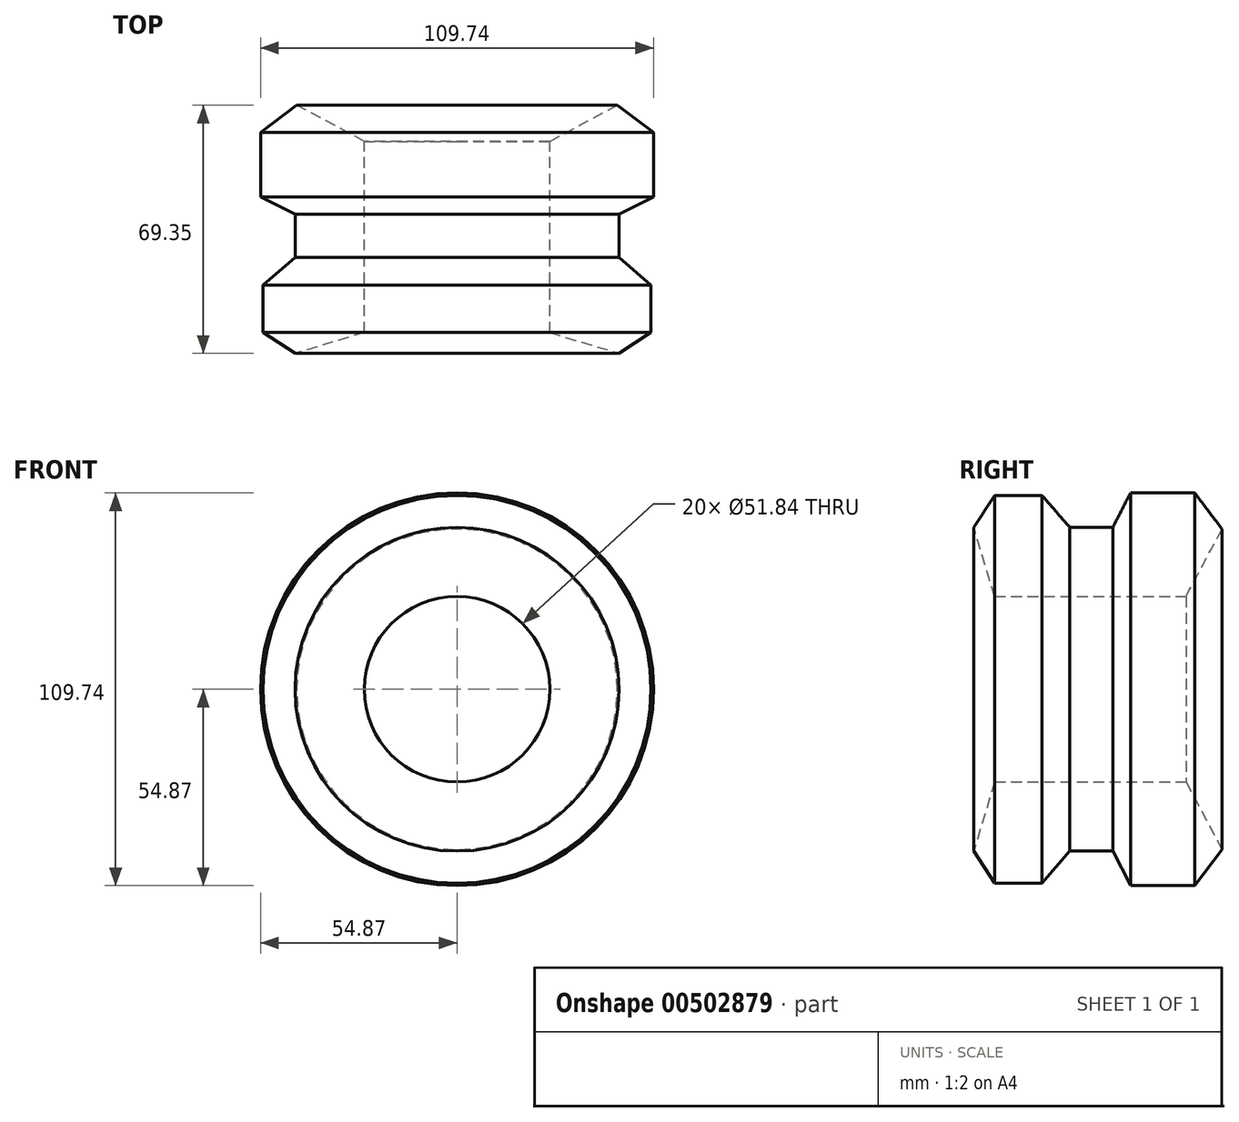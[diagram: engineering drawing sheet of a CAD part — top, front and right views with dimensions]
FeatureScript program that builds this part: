
annotation { "Feature Type Name" : "Feature", "Feature Type Description" : "" }
export const myFeature = defineFeature(function(context is Context, id is Id, definition is map)
    precondition{}
    {
        {
            var Q0;
            Q0=qCreatedBy(makeId("Top.planeOp"),FACE);
            var sketch = newSketch(context, id + "F0", { "sketchPlane" : qUnion([Q0])});
            skLineSegment(sketch, "E0", {"start": v(-44.77, 42.53) * mm, "end": v(-54.87, 34.9) * mm});
            skLineSegment(sketch, "E1", {"start": v(-54.87, 34.9) * mm, "end": v(-54.87, 16.94) * mm});
            skLineSegment(sketch, "E2", {"start": v(-54.87, 16.94) * mm, "end": v(-45.22, 12) * mm});
            skLineSegment(sketch, "E3", {"start": v(-45.22, 12) * mm, "end": v(-45.22, 0) * mm});
            skLineSegment(sketch, "E4", {"start": v(-45.22, 0) * mm, "end": v(-54.2, -7.74) * mm});
            skLineSegment(sketch, "E5", {"start": v(-54.2, -7.74) * mm, "end": v(-54.2, -20.98) * mm});
            skLineSegment(sketch, "E6", {"start": v(-54.2, -20.98) * mm, "end": v(-45.22, -26.82) * mm});
            skLineSegment(sketch, "E7", {"start": v(-45.22, -26.82) * mm, "end": v(-25.92, -20.98) * mm});
            skLineSegment(sketch, "E8", {"start": v(-25.92, -20.98) * mm, "end": v(-25.92, 0) * mm});
            skLineSegment(sketch, "E9", {"start": v(-25.92, 0) * mm, "end": v(-25.92, 32.43) * mm});
            skLineSegment(sketch, "E10", {"start": v(-25.92, 32.43) * mm, "end": v(-44.77, 42.53) * mm});
            skLineSegment(sketch, "E11", {"start": v(0, 0) * mm, "end": v(0, 18.74) * mm});
            skLineSegment(sketch, "E12", {"start": v(0, 18.74) * mm, "end": v(0, 0) * mm});
            skSolve(sketch);
        }
        {
            var Q0;
            Q0=makeQuery(id+"F0.imprint","IMPRINT",FACE,{"disambiguationData":[TD([[makeQuery(id+"F0.imprint","IMPRINT",EDGE,{"derivedFrom":sQuery(id+"F0.wireOp",EDGE,"E0")}),1.0]])]});
            var Q1;
            Q1=sQuery(id+"F0.wireOp",EDGE,"E12");
            revolve(context, id + "F1", {"entities" : qUnion([Q0]), "axis" : qUnion([Q1]), "revolveType" : RevolveType.FULL});
        }
    });
